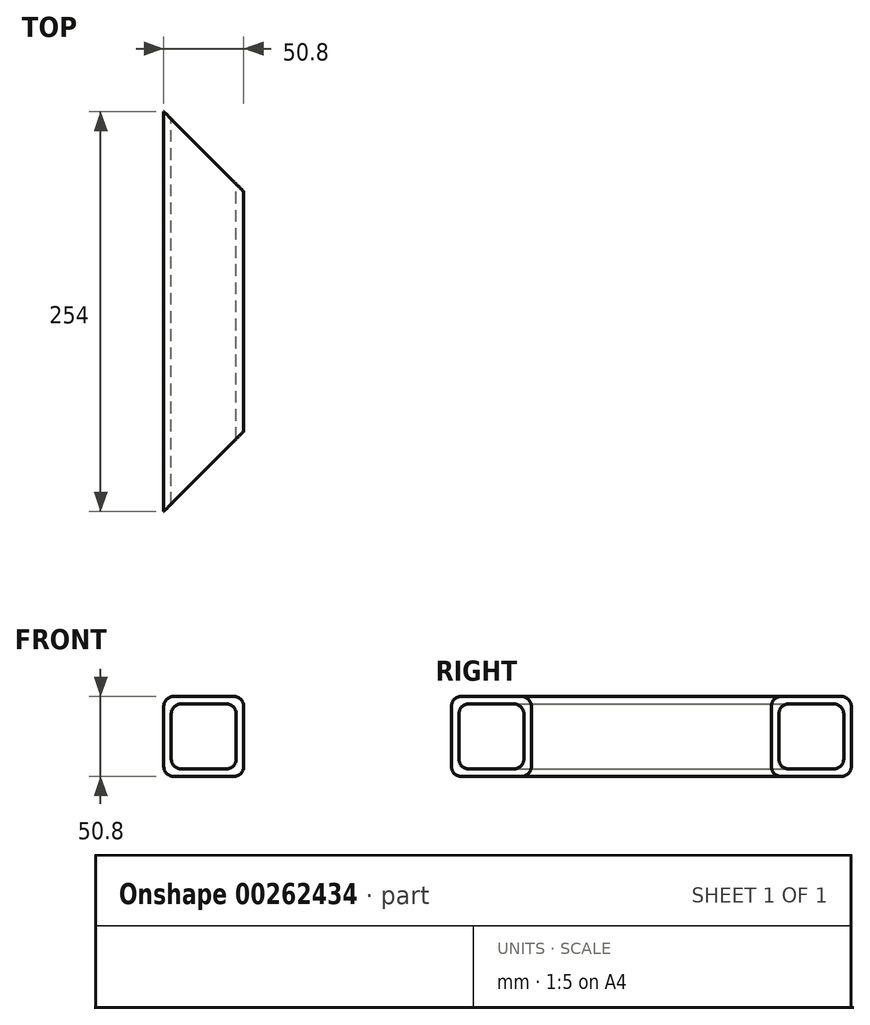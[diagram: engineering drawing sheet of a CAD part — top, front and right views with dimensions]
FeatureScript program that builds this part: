
annotation { "Feature Type Name" : "Feature", "Feature Type Description" : "" }
export const myFeature = defineFeature(function(context is Context, id is Id, definition is map)
    precondition{}
    {
        {
            var Q0;
            Q0=qCreatedBy(makeId("Front.planeOp"),FACE);
            var sketch = newSketch(context, id + "F0", { "sketchPlane" : qUnion([Q0])});
            skLineSegment(sketch, "E0.bottom", {"start": v(14.29, 20.64) * mm, "end": v(-14.29, 20.64) * mm});
            skLineSegment(sketch, "E0.top", {"start": v(14.29, -20.64) * mm, "end": v(-14.29, -20.64) * mm});
            skLineSegment(sketch, "E0.left", {"start": v(20.64, 14.29) * mm, "end": v(20.64, -14.29) * mm});
            skLineSegment(sketch, "E0.right", {"start": v(-20.64, 14.29) * mm, "end": v(-20.64, -14.29) * mm});
            skPoint(sketch, "E0.middle", {"position": v(0, 0) * mm});
            skLineSegment(sketch, "E1.bottom", {"start": v(19.05, 25.4) * mm, "end": v(-19.05, 25.4) * mm});
            skLineSegment(sketch, "E1.top", {"start": v(19.05, -25.4) * mm, "end": v(-19.05, -25.4) * mm});
            skLineSegment(sketch, "E1.left", {"start": v(25.4, 19.05) * mm, "end": v(25.4, -19.05) * mm});
            skLineSegment(sketch, "E1.right", {"start": v(-25.4, 19.05) * mm, "end": v(-25.4, -19.05) * mm});
            skPoint(sketch, "E2.visualSharp", {"position": v(-25.4, 25.4) * mm});
            skArc(sketch, "E2.filletArc", {"start": v(-19.05, 25.4) * mm, "mid": v(-23.54, 23.54) * mm, "end": v(-25.4, 19.05) * mm});
            skPoint(sketch, "E3.visualSharp", {"position": v(-20.64, 20.64) * mm});
            skArc(sketch, "E3.filletArc", {"start": v(-14.29, 20.64) * mm, "mid": v(-18.78, 18.78) * mm, "end": v(-20.64, 14.29) * mm});
            skPoint(sketch, "E4.visualSharp", {"position": v(-25.4, -25.4) * mm});
            skArc(sketch, "E4.filletArc", {"start": v(-25.4, -19.05) * mm, "mid": v(-23.54, -23.54) * mm, "end": v(-19.05, -25.4) * mm});
            skPoint(sketch, "E5.visualSharp", {"position": v(-20.64, -20.64) * mm});
            skArc(sketch, "E5.filletArc", {"start": v(-20.64, -14.29) * mm, "mid": v(-18.78, -18.78) * mm, "end": v(-14.29, -20.64) * mm});
            skPoint(sketch, "E6.visualSharp", {"position": v(20.64, -20.64) * mm});
            skArc(sketch, "E6.filletArc", {"start": v(14.29, -20.64) * mm, "mid": v(18.78, -18.78) * mm, "end": v(20.64, -14.29) * mm});
            skPoint(sketch, "E7.visualSharp", {"position": v(25.4, -25.4) * mm});
            skArc(sketch, "E7.filletArc", {"start": v(19.05, -25.4) * mm, "mid": v(23.54, -23.54) * mm, "end": v(25.4, -19.05) * mm});
            skPoint(sketch, "E8.visualSharp", {"position": v(25.4, 25.4) * mm});
            skArc(sketch, "E8.filletArc", {"start": v(25.4, 19.05) * mm, "mid": v(23.54, 23.54) * mm, "end": v(19.05, 25.4) * mm});
            skPoint(sketch, "E9.visualSharp", {"position": v(20.64, 20.64) * mm});
            skArc(sketch, "E9.filletArc", {"start": v(20.64, 14.29) * mm, "mid": v(18.78, 18.78) * mm, "end": v(14.29, 20.64) * mm});
            skSolve(sketch);
        }
        {
            var Q0;
            Q0 = qSketchRegion(id + "F0", true);
            extrude(context, id + "F1", {"entities" : qUnion([Q0]), "depth" : 254 * mm});
        }
        {
            var Q0;
            Q0=qCreatedBy(makeId("Top.planeOp"),FACE);
            var sketch = newSketch(context, id + "F2", { "sketchPlane" : qUnion([Q0])});
            skLineSegment(sketch, "E10.bottom", {"start": v(25.4, 0) * mm, "end": v(-25.4, 0) * mm});
            skLineSegment(sketch, "E10.left", {"start": v(25.4, 0) * mm, "end": v(25.4, -50.8) * mm});
            skPoint(sketch, "E10.middle", {"position": v(0, -25.4) * mm});
            skLineSegment(sketch, "E11", {"start": v(-25.4, 0) * mm, "end": v(25.4, -50.8) * mm});
            skPoint(sketch, "E10.top.end.orphan", {"position": v(-25.4, -50.8) * mm});
            skLineSegment(sketch, "E12.top", {"start": v(25.4, -254) * mm, "end": v(-25.4, -254) * mm});
            skLineSegment(sketch, "E12.left", {"start": v(25.4, -203.2) * mm, "end": v(25.4, -254) * mm});
            skPoint(sketch, "E12.middle", {"position": v(0, -228.6) * mm});
            skLineSegment(sketch, "E13", {"start": v(-25.4, -254) * mm, "end": v(25.4, -203.2) * mm});
            skPoint(sketch, "E12.right.start.orphan", {"position": v(-25.4, -203.2) * mm});
            skSolve(sketch);
        }
        {
            var Q0;
            Q0 = qSketchRegion(id + "F2", true);
            extrude(context, id + "F3", {"entities" : qUnion([Q0]), "operationType" : NewBodyOperationType.REMOVE, "endBound" : BoundingType.THROUGH_ALL, "oppositeDirection" : true, "depth" : 25.4 * mm, "hasSecondDirection" : true, "secondDirectionOppositeDirection" : false, "secondDirectionDepth" : 25.4 * mm});
        }
    });
